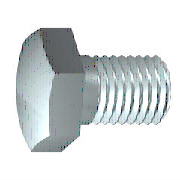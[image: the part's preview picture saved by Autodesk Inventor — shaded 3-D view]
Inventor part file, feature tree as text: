
AUTODESK INVENTOR PART (.ipt)
format: ipt  version: 2013 (Build 170138000, 138)  size: 187,392 bytes
history: native  units: mm (DEFAULTED — no unit token found)
features: sketch x2, extrude x1, chamfer x1, plane x1
ambient origin geometry x7: Origin, YZ Plane, XZ Plane, X Axis, Y Axis, Z Axis, Center Point
bodies: Solid1 (feature_tree), Body (feature_tree)
feature tree (5):
  extrude  "Head"  TaperAngle=90.0deg  [1 undecoded]
  chamfer  "Chamfer1"  [1 undecoded]
  plane  "Work Plane1"
  sketch  "Sketch1"  dims[d2=8.0mm d12=90.0deg]
  sketch  "Sketch2"  dims[d3=5.68mm d4=0.0mm d21=90.0deg d6=0.766813mm d7=0.766912mm d8=0.0mm d11=13.0mm d15=22.0mm d16=0.0mm d55=45.0deg d58=0.0mm d59=85.0mm d65=13.0mm d67=30.0deg d68=15.6mm d69=5.68mm d71=0.1mm d73=0.0mm]
note: 2 required parameter values undecoded (feature->parameter linkage not recoverable at this tier; creation-order binding heuristic only, values carry confidence <= 0.55)
